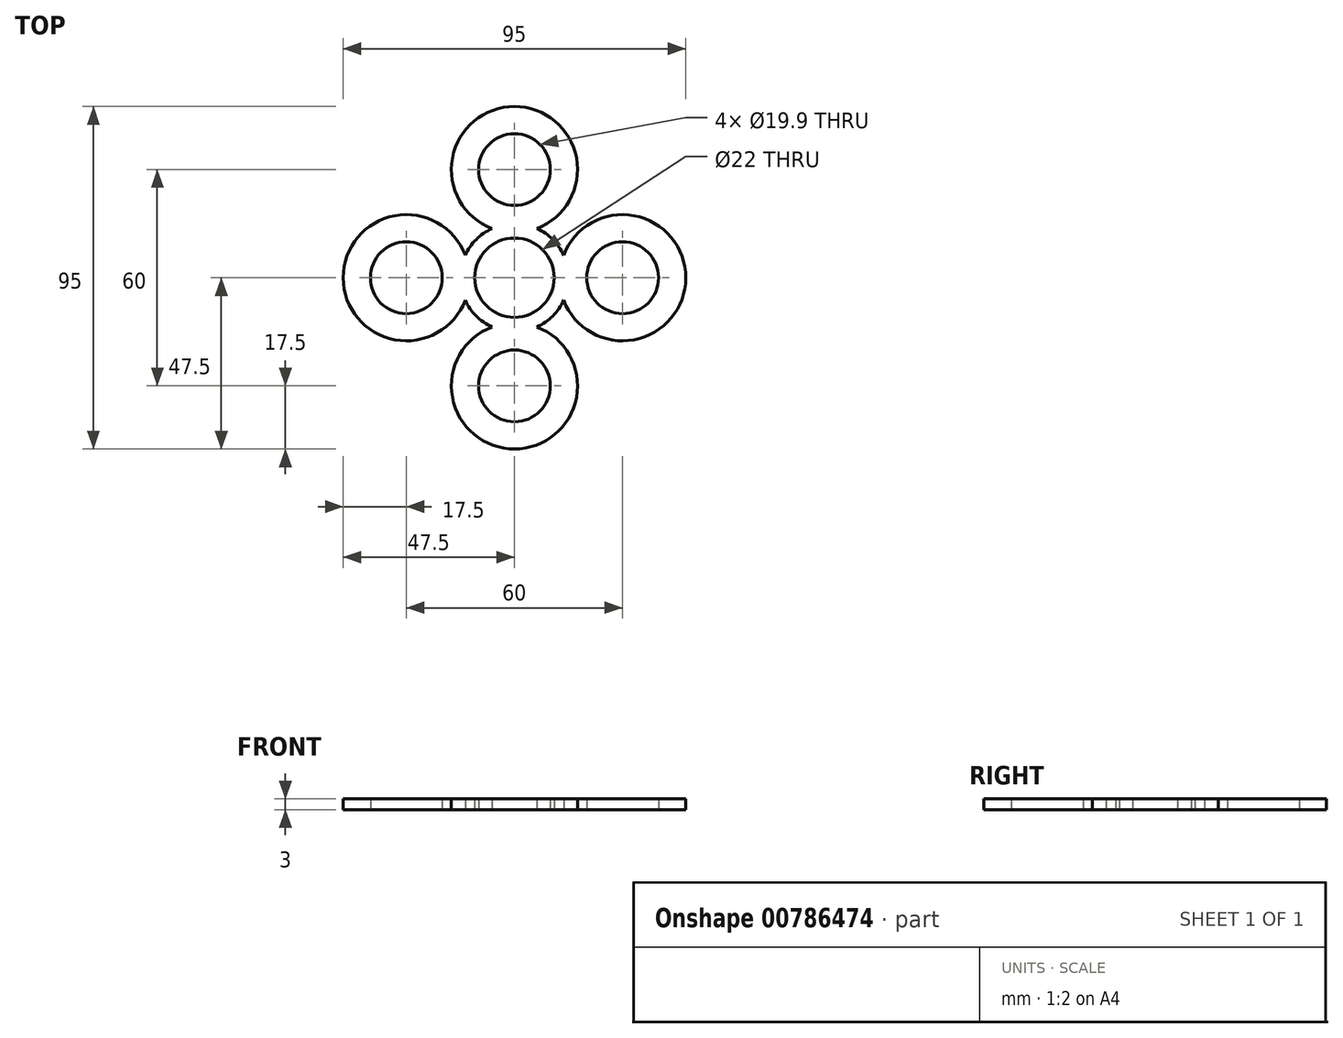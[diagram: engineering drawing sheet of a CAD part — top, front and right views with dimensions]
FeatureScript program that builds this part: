
annotation { "Feature Type Name" : "Feature", "Feature Type Description" : "" }
export const myFeature = defineFeature(function(context is Context, id is Id, definition is map)
    precondition{}
    {
        {
            var Q0;
            Q0=qCreatedBy(makeId("Top.planeOp"),FACE);
            var sketch = newSketch(context, id + "F0", { "sketchPlane" : qUnion([Q0])});
            skPoint(sketch, "E0.center", {"position": v(0, 0) * mm});
            skArc(sketch, "E1", {"start": v(7.78, 7.78) * mm, "mid": v(0, 11) * mm, "end": v(-7.78, 7.78) * mm});
            skArc(sketch, "E2", {"start": v(-6.23, 13.65) * mm, "mid": v(-8.55, 12.32) * mm, "end": v(-10.6, 10.6) * mm});
            skCircle(sketch, "E3", {"center": v(0, 30) * mm, "radius": 9.95 * mm});
            skArc(sketch, "E4", {"start": v(6.23, 13.65) * mm, "mid": v(0, 47.5) * mm, "end": v(-6.23, 13.65) * mm});
            skArc(sketch, "E5.trimOffspring", {"start": v(10.6, 10.6) * mm, "mid": v(8.55, 12.32) * mm, "end": v(6.23, 13.65) * mm});
            skCircle(sketch, "E6.1.0", {"center": v(-30, 0) * mm, "radius": 9.95 * mm});
            skArc(sketch, "E6.1.1", {"start": v(-13.65, 6.23) * mm, "mid": v(-47.5, 0) * mm, "end": v(-13.65, -6.23) * mm});
            skArc(sketch, "E6.1.2", {"start": v(-13.65, -6.23) * mm, "mid": v(-12.32, -8.55) * mm, "end": v(-10.6, -10.6) * mm});
            skArc(sketch, "E6.1.3", {"start": v(-10.6, 10.6) * mm, "mid": v(-12.32, 8.55) * mm, "end": v(-13.65, 6.23) * mm});
            skArc(sketch, "E6.1.4", {"start": v(-7.78, 7.78) * mm, "mid": v(-11, 0) * mm, "end": v(-7.78, -7.78) * mm});
            skCircle(sketch, "E6.2.0", {"center": v(0, -30) * mm, "radius": 9.95 * mm});
            skArc(sketch, "E6.2.1", {"start": v(-6.23, -13.65) * mm, "mid": v(0, -47.5) * mm, "end": v(6.23, -13.65) * mm});
            skArc(sketch, "E6.2.2", {"start": v(6.23, -13.65) * mm, "mid": v(8.55, -12.32) * mm, "end": v(10.6, -10.6) * mm});
            skArc(sketch, "E6.2.3", {"start": v(-10.6, -10.6) * mm, "mid": v(-8.55, -12.32) * mm, "end": v(-6.23, -13.65) * mm});
            skArc(sketch, "E6.2.4", {"start": v(-7.78, -7.78) * mm, "mid": v(0, -11) * mm, "end": v(7.78, -7.78) * mm});
            skCircle(sketch, "E6.3.0", {"center": v(30, 0) * mm, "radius": 9.95 * mm});
            skArc(sketch, "E6.3.1", {"start": v(13.65, -6.23) * mm, "mid": v(47.5, 0) * mm, "end": v(13.65, 6.23) * mm});
            skArc(sketch, "E6.3.2", {"start": v(13.65, 6.23) * mm, "mid": v(12.32, 8.55) * mm, "end": v(10.6, 10.6) * mm});
            skArc(sketch, "E6.3.3", {"start": v(10.6, -10.6) * mm, "mid": v(12.32, -8.55) * mm, "end": v(13.65, -6.23) * mm});
            skArc(sketch, "E6.3.4", {"start": v(7.78, -7.78) * mm, "mid": v(11, 0) * mm, "end": v(7.78, 7.78) * mm});
            skSolve(sketch);
        }
        {
            var Q0;
            Q0 = qSketchRegion(id + "F0", true);
            extrude(context, id + "F1", {"entities" : qUnion([Q0]), "depth" : 3 * mm, "offsetDistance" : 25 * mm});
        }
    });
